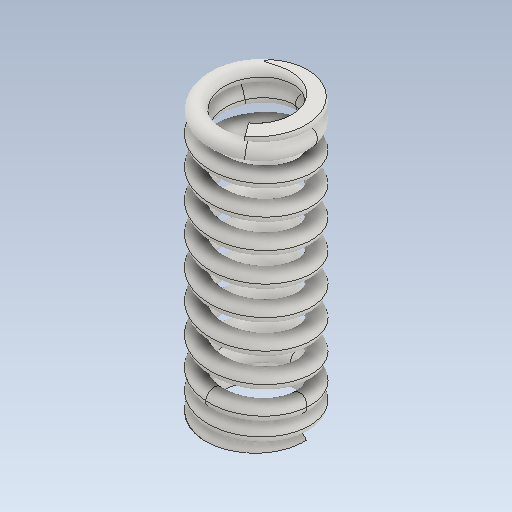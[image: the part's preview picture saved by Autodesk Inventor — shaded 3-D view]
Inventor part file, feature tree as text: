
AUTODESK INVENTOR PART (.ipt)
format: ipt  version: 2020 (Build 240168000, 168)  size: 1,045,504 bytes
history: native  units: in
note: dims shown in document units (in); Inventor stores cm internally (conversion verified against a paired STEP export)
features: other x56, sketch x3, helix x2, plane x1
ambient origin geometry x8: Origin, YZ Plane, XZ Plane, XY Plane, X Axis, Y Axis, Z Axis, Center Point
bodies: Solid1 (feature_tree)
feature tree (62):
  other  "Compress Spring1"
  other  "Solid1::Compress Spring1"
  other  "TaggingFeature1"
  other  "Path Section Sketch(Right)"
  helix  "Coil Section Sketch(Right)"  [1 undecoded]
  other  "Start Transition Coil Sketch 1(Right)"
  sketch  "Sketch  Start Transition 2(R)"
  sketch  "Sketch  Start Transition 3(R)"
  sketch  "Sketch  Start Transition 4(R)"
  other  "Start Ends Skecth(Right)"
  other  "Start Cut Sketch(Right)"
  other  "End Transition Coil Sketch 1(Right)"
  other  "End Transition Coil Sketch 2(Right)"
  other  "End Transition Coil Sketch 3(Right)"
  other  "End Transition Coil Sketch 4(Right)"
  other  "End Coil Skecth(Right)"
  other  "End Cut Sketch(Right)"
  other  "Plain Ends Cut Sketch 1(Right)"
  other  "Plain Ends Cut Sketch 2(Right)"
  other  "Path Section Sketch(Left)"
  helix  "Coil Section Sketch(Left)"  [1 undecoded]
  other  "Start Transition Coil Sketch 1(Left)"
  other  "Start Transition Coil Sketch 2(Left)"
  other  "Start Transition Coil Sketch 3(Left)"
  other  "Start Transition Coil Sketch 4(Left)"
  other  "Start Ends Skecth(Left)"
  other  "Start Cut Sketch(Left)"
  other  "End Transition Coil Sketch 1(Left)"
  other  "End Transition Coil Sketch 2(Left)"
  other  "End Transition Coil Sketch 3(Left)"
  other  "End Transition Coil Sketch 4(Left)"
  other  "End Coil Skecth(Left)"
  other  "End Cut Sketch(Left)"
  other  "Plain Ends Cut Sketch 1(Left)"
  other  "Plain Ends Cut Sketch 2(Left)"
  other  "Main Coil Path(Right)"
  other  "Main Coil Path(Left)"
  other  "Section Work Plane(Right)"
  other  "Start Work Plane(Right)"
  other  "End Work Plane(Right)"
  other  "End Cut Work Plane(Right)"
  other  "Start Cut Work Plane(Right)"
  other  "Plain Ends Cut Work Plane 1(Right)"
  other  "Plain Ends Cut Work Plane 2(Right)"
  other  "Section Work Plane(Left)"
  other  "Start Work Plane(Left)"
  other  "End Work Plane(Left)"
  other  "End Cut Work Plane(Left)"
  other  "Start Cut Work Plane(Left)"
  other  "Plain Ends Cut Work Plane 1(Left)"
  other  "Plain Ends Cut Work Plane 2(Left)"
  other  "iMate Based Work Plane"
  plane  "Work Plane Start Section"
  other  "Y Axis_1"
  other  "Preview X Axis"
  other  "Preview Center Point"
  other  "Srf1"
  other  "Srf2"
  other  "Srf1::Derived"
  other  "Srf2::Derived"
  other  "Planar"
  other  "Axial"
note: 2 required parameter values undecoded (feature->parameter linkage not recoverable at this tier; creation-order binding heuristic only, values carry confidence <= 0.55)
